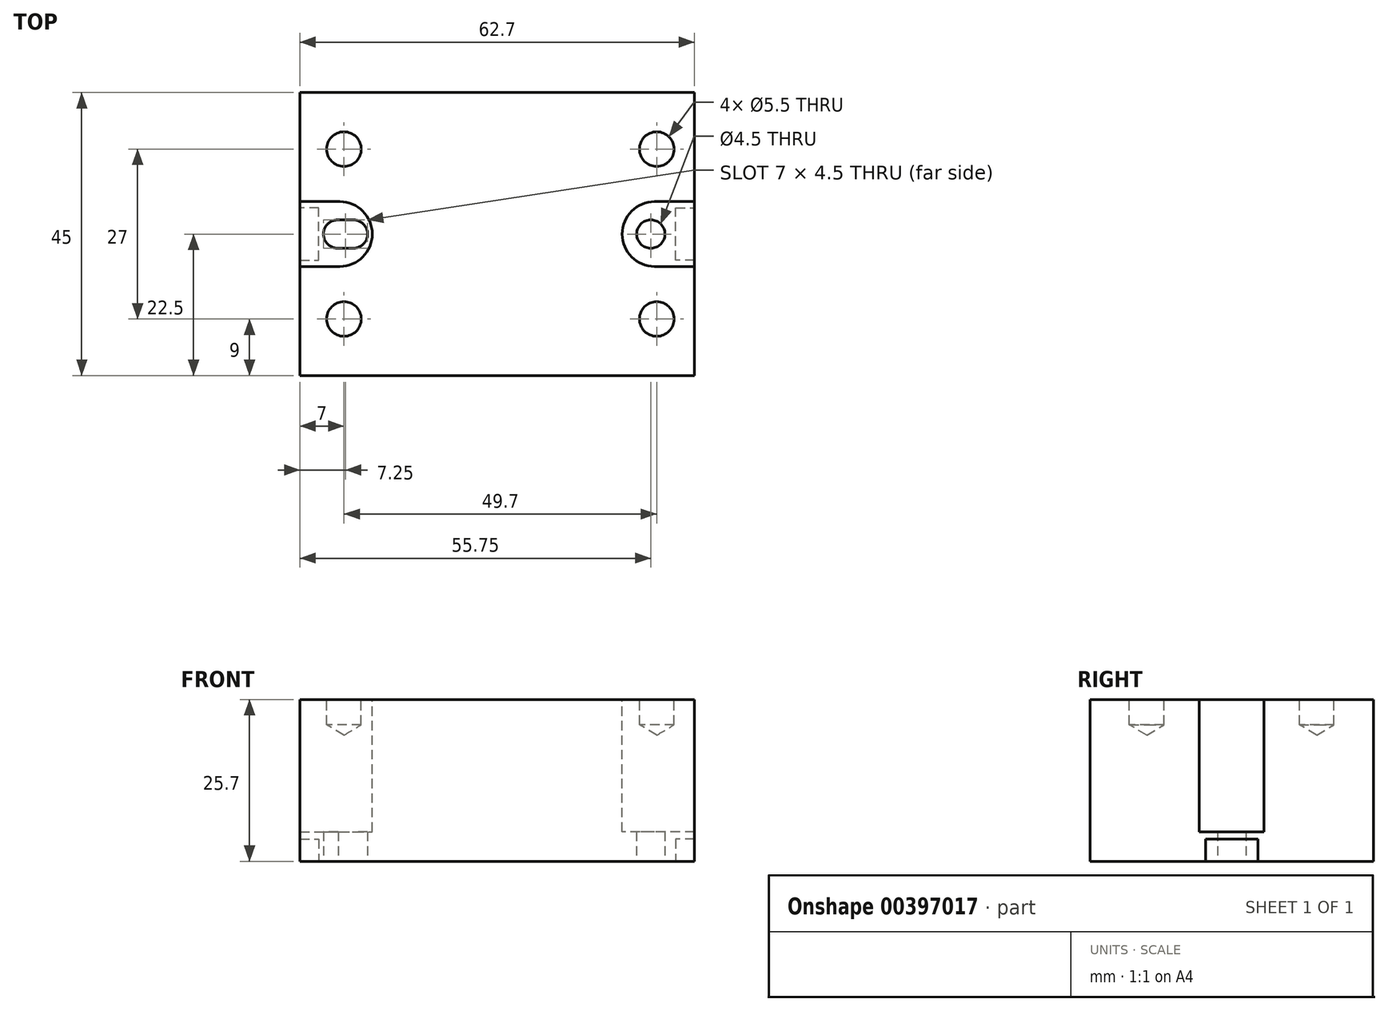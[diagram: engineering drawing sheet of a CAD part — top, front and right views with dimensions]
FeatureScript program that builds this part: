
annotation { "Feature Type Name" : "Feature", "Feature Type Description" : "" }
export const myFeature = defineFeature(function(context is Context, id is Id, definition is map)
    precondition{}
    {
        {
            var Q0;
            Q0=qCreatedBy(makeId("Top.planeOp"),FACE);
            var sketch = newSketch(context, id + "F0", { "sketchPlane" : qUnion([Q0])});
            skLineSegment(sketch, "E0.bottom", {"start": v(0, 0) * mm, "end": v(62.7, 0) * mm});
            skLineSegment(sketch, "E0.top", {"start": v(0, 45) * mm, "end": v(62.7, 45) * mm});
            skLineSegment(sketch, "E0.left", {"start": v(0, 0) * mm, "end": v(0, 45) * mm});
            skLineSegment(sketch, "E0.right", {"start": v(62.7, 0) * mm, "end": v(62.7, 45) * mm});
            skSolve(sketch);
        }
        {
            var Q0;
            Q0 = qSketchRegion(id + "F0", true);
            extrude(context, id + "F1", {"entities" : qUnion([Q0]), "depth" : 25.7 * mm});
        }
        {
            var Q0;
            Q0=makeQuery(id+"F1.opExtrude","CAP_FACE",FACE,{"disambiguationData":[OSD([sQuery(id+"F0.wireOp",EDGE,"E0.bottom"),sQuery(id+"F0.wireOp",EDGE,"E0.top"),sQuery(id+"F0.wireOp",EDGE,"E0.left"),sQuery(id+"F0.wireOp",EDGE,"E0.right")])],"isStart":true});
            var sketch = newSketch(context, id + "F2", { "sketchPlane" : qUnion([Q0])});
            skLineSegment(sketch, "E1", {"start": v(31.35, 0) * mm, "end": v(31.35, -45) * mm, "construction": true});
            skLineSegment(sketch, "E2", {"start": v(0, -22.5) * mm, "end": v(62.7, -22.5) * mm, "construction": true});
            skLineSegment(sketch, "E3", {"start": v(0, -22.5) * mm, "end": v(0, -18.35) * mm});
            skLineSegment(sketch, "E4", {"start": v(0, -18.35) * mm, "end": v(3, -18.35) * mm});
            skLineSegment(sketch, "E5", {"start": v(3, -18.35) * mm, "end": v(3, -22.5) * mm});
            skLineSegment(sketch, "E6", {"start": v(3, -22.5) * mm, "end": v(3, -26.65) * mm});
            skLineSegment(sketch, "E7", {"start": v(3, -26.65) * mm, "end": v(0, -26.65) * mm});
            skLineSegment(sketch, "E8", {"start": v(0, -26.65) * mm, "end": v(0, -22.5) * mm});
            skLineSegment(sketch, "E9.MirrorCS", {"start": v(62.7, -18.35) * mm, "end": v(59.7, -18.35) * mm});
            skLineSegment(sketch, "E10.MirrorCS", {"start": v(62.7, -22.5) * mm, "end": v(62.7, -18.35) * mm});
            skLineSegment(sketch, "E11.MirrorCS", {"start": v(62.7, -26.65) * mm, "end": v(62.7, -22.5) * mm});
            skLineSegment(sketch, "E12.MirrorCS", {"start": v(59.7, -26.65) * mm, "end": v(62.7, -26.65) * mm});
            skLineSegment(sketch, "E13.MirrorCS", {"start": v(59.7, -22.5) * mm, "end": v(59.7, -26.65) * mm});
            skLineSegment(sketch, "E14.MirrorCS", {"start": v(59.7, -18.35) * mm, "end": v(59.7, -22.5) * mm});
            skSolve(sketch);
        }
        {
            var Q0;
            Q0 = qSketchRegion(id + "F2", true);
            extrude(context, id + "F3", {"entities" : qUnion([Q0]), "operationType" : NewBodyOperationType.REMOVE, "oppositeDirection" : true, "depth" : 3.5 * mm});
        }
        {
            var Q0;
            Q0=makeQuery(id+"F1.opExtrude","CAP_FACE",FACE,{"disambiguationData":[OSD([sQuery(id+"F0.wireOp",EDGE,"E0.bottom"),sQuery(id+"F0.wireOp",EDGE,"E0.top"),sQuery(id+"F0.wireOp",EDGE,"E0.left"),sQuery(id+"F0.wireOp",EDGE,"E0.right")])],"isStart":false});
            var sketch = newSketch(context, id + "F4", { "sketchPlane" : qUnion([Q0])});
            skLineSegment(sketch, "E15", {"start": v(0, 22.5) * mm, "end": v(62.7, 22.5) * mm, "construction": true});
            skLineSegment(sketch, "E16", {"start": v(31.35, 45) * mm, "end": v(31.35, 0) * mm, "construction": true});
            skLineSegment(sketch, "E17", {"start": v(0, 22.5) * mm, "end": v(0, 27.65) * mm});
            skLineSegment(sketch, "E18", {"start": v(0, 27.65) * mm, "end": v(6.35, 27.65) * mm});
            skLineSegment(sketch, "E19.MirrorCS", {"start": v(0, 22.5) * mm, "end": v(0, 17.35) * mm});
            skLineSegment(sketch, "E20.MirrorCS", {"start": v(0, 17.35) * mm, "end": v(6.35, 17.35) * mm});
            skArc(sketch, "E21", {"start": v(6.35, 17.35) * mm, "mid": v(11.5, 22.5) * mm, "end": v(6.35, 27.65) * mm});
            skArc(sketch, "E22.MirrorCS", {"start": v(56.35, 17.35) * mm, "mid": v(51.2, 22.5) * mm, "end": v(56.35, 27.65) * mm});
            skLineSegment(sketch, "E23.MirrorCS", {"start": v(62.7, 27.65) * mm, "end": v(56.35, 27.65) * mm});
            skLineSegment(sketch, "E24.MirrorCS", {"start": v(62.7, 22.5) * mm, "end": v(62.7, 27.65) * mm});
            skLineSegment(sketch, "E25.MirrorCS", {"start": v(62.7, 22.5) * mm, "end": v(62.7, 17.35) * mm});
            skLineSegment(sketch, "E26.MirrorCS", {"start": v(62.7, 17.35) * mm, "end": v(56.35, 17.35) * mm});
            skSolve(sketch);
        }
        {
            var Q0;
            Q0 = qSketchRegion(id + "F4", true);
            extrude(context, id + "F5", {"entities" : qUnion([Q0]), "operationType" : NewBodyOperationType.REMOVE, "oppositeDirection" : true, "depth" : 21 * mm});
        }
        {
            var Q0;
            Q0=makeQuery(id+"F1.opExtrude","CAP_FACE",FACE,{"disambiguationData":[OSD([sQuery(id+"F0.wireOp",EDGE,"E0.bottom"),sQuery(id+"F0.wireOp",EDGE,"E0.top"),sQuery(id+"F0.wireOp",EDGE,"E0.left"),sQuery(id+"F0.wireOp",EDGE,"E0.right")])],"isStart":true});
            var sketch = newSketch(context, id + "F6", { "sketchPlane" : qUnion([Q0])});
            skLineSegment(sketch, "E27", {"start": v(0, -22.5) * mm, "end": v(62.7, -22.5) * mm, "construction": true});
            skPoint(sketch, "E27.startSnap0", {"position": v(3, -22.5) * mm});
            skPoint(sketch, "E27.endSnap0", {"position": v(59.7, -22.5) * mm});
            skPoint(sketch, "E27.endSnap1", {"position": v(62.7, -35.83) * mm});
            skLineSegment(sketch, "E28", {"start": v(31.35, 0) * mm, "end": v(31.35, -45) * mm, "construction": true});
            skCircle(sketch, "E29", {"center": v(55.75, -22.5) * mm, "radius": 2.25 * mm});
            skArc(sketch, "E30", {"start": v(6.01, -20.25) * mm, "mid": v(3.75, -22.54) * mm, "end": v(6.09, -24.75) * mm});
            skArc(sketch, "E31", {"start": v(8.5, -24.75) * mm, "mid": v(10.75, -22.5) * mm, "end": v(8.5, -20.25) * mm});
            skLineSegment(sketch, "E32", {"start": v(6.01, -20.25) * mm, "end": v(8.5, -20.25) * mm});
            skLineSegment(sketch, "E33", {"start": v(6.09, -24.75) * mm, "end": v(8.5, -24.75) * mm});
            skSolve(sketch);
        }
        {
            var Q0;
            Q0 = qSketchRegion(id + "F6", true);
            extrude(context, id + "F7", {"entities" : qUnion([Q0]), "operationType" : NewBodyOperationType.REMOVE, "endBound" : BoundingType.UP_TO_NEXT, "oppositeDirection" : true, "depth" : 25 * mm});
        }
        {
            var Q0;
            Q0=makeQuery(id+"F1.opExtrude","CAP_FACE",FACE,{"disambiguationData":[OSD([sQuery(id+"F0.wireOp",EDGE,"E0.bottom"),sQuery(id+"F0.wireOp",EDGE,"E0.top"),sQuery(id+"F0.wireOp",EDGE,"E0.left"),sQuery(id+"F0.wireOp",EDGE,"E0.right")])],"isStart":false});
            var sketch = newSketch(context, id + "F8", { "sketchPlane" : qUnion([Q0])});
            skLineSegment(sketch, "E34", {"start": v(62.7, 22.5) * mm, "end": v(0, 22.5) * mm, "construction": true});
            skPoint(sketch, "E34.startSnap0", {"position": v(51.2, 22.5) * mm});
            skPoint(sketch, "E34.endSnap0", {"position": v(0, 36.33) * mm});
            skLineSegment(sketch, "E35", {"start": v(31.35, 45) * mm, "end": v(31.35, 0) * mm, "construction": true});
            skPoint(sketch, "E36", {"position": v(7, 9) * mm});
            skPoint(sketch, "E37", {"position": v(56.7, 9) * mm});
            skPoint(sketch, "E38.MirrorP", {"position": v(7, 36) * mm});
            skPoint(sketch, "E39.MirrorP", {"position": v(56.7, 36) * mm});
            skSolve(sketch);
        }
        {
            var Q0;
            Q0=sQuery(id+"F8.wireOp",VERTEX,"E38.MirrorP");
            var Q1;
            Q1=sQuery(id+"F8.wireOp",VERTEX,"E36");
            var Q2;
            Q2=sQuery(id+"F8.wireOp",VERTEX,"E37");
            var Q3;
            Q3=sQuery(id+"F8.wireOp",VERTEX,"E39.MirrorP");
            var Q4;
            Q4=makeQuery(id+"F1.opExtrude","SWEPT_BODY",BODY,{"disambiguationData":[OSD([sQuery(id+"F0.wireOp",EDGE,"E0.bottom"),sQuery(id+"F0.wireOp",EDGE,"E0.top"),sQuery(id+"F0.wireOp",EDGE,"E0.left"),sQuery(id+"F0.wireOp",EDGE,"E0.right")])]});
            hole(context, id + "F9", {"style" : HoleStyle.SIMPLE, "endStyle" : HoleEndStyle.BLIND, "standardTappedOrClearance" : lookupTablePath({ "standard" : "ISO", "fit" : "Normal", "size" : "M5", "type" : "Clearance" }), "standardBlindInLast" : lookupTablePath({ "fit" : "Standard", "standard" : "ISO", "size" : "M5", "type" : "Clearance" }), "holeDiameter" : 5.5 * mm, "holeDepth" : 4 * mm, "isTappedThrough" : true, "tappedDepth" : 12 * mm, "tapClearance" : 3, "startFromSketch" : true, "locations" : qUnion([Q0, Q1, Q2, Q3]), "scope" : qUnion([Q4])});
        }
    });
